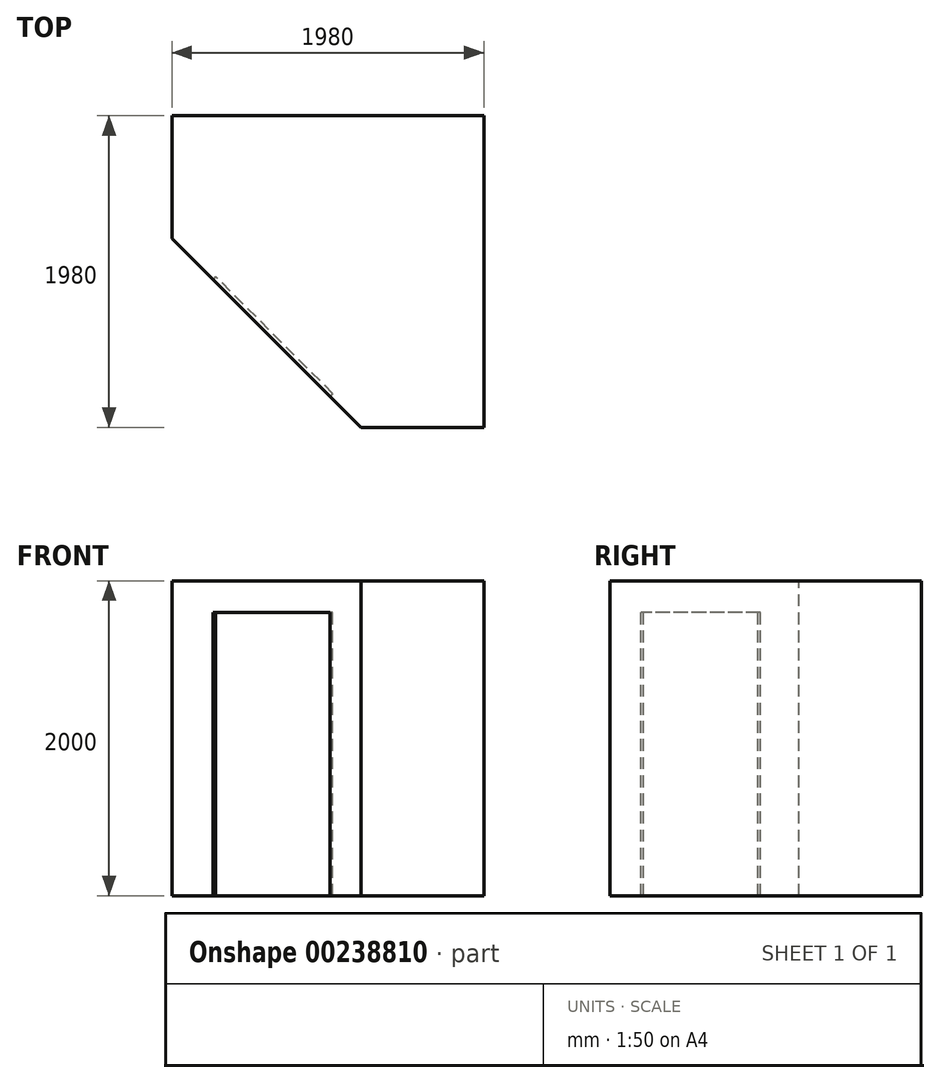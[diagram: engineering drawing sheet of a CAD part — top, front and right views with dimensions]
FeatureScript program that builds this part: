
annotation { "Feature Type Name" : "Feature", "Feature Type Description" : "" }
export const myFeature = defineFeature(function(context is Context, id is Id, definition is map)
    precondition{}
    {
        {
            var Q0;
            Q0=qCreatedBy(makeId("Top.planeOp"),FACE);
            var sketch = newSketch(context, id + "F0", { "sketchPlane" : qUnion([Q0])});
            skLineSegment(sketch, "E0.bottom", {"start": v(0, 0) * mm, "end": v(1980, 0) * mm});
            skLineSegment(sketch, "E0.top", {"start": v(0, 1980) * mm, "end": v(1980, 1980) * mm});
            skLineSegment(sketch, "E0.left", {"start": v(0, 0) * mm, "end": v(0, 1980) * mm});
            skLineSegment(sketch, "E0.right", {"start": v(1980, 0) * mm, "end": v(1980, 1980) * mm});
            skSolve(sketch);
        }
        {
            var Q0;
            Q0 = qSketchRegion(id + "F0", true);
            extrude(context, id + "F1", {"entities" : qUnion([Q0]), "depth" : 2000 * mm});
        }
        {
            var Q0;
            Q0=makeQuery(id+"F1.opExtrude","SWEPT_EDGE",EDGE,{"disambiguationData":[OSD([sQuery(id+"F0.wireOp",EDGE,"E0.bottom"),sQuery(id+"F0.wireOp",EDGE,"E0.left")])]});
            chamfer(context, id + "F2", {"entities" : qUnion([Q0]), "width" : 1200 * mm, "tangentPropagation" : true});
        }
        {
            var Q0;
            Q0=makeQuery(id+"F2.opChamfer","BLEND_FACE",FACE,{"disambiguationData":[OSD([sQuery(id+"F0.wireOp",EDGE,"E0.bottom"),sQuery(id+"F0.wireOp",EDGE,"E0.left")])]});
            var sketch = newSketch(context, id + "F3", { "sketchPlane" : qUnion([Q0])});
            skLineSegment(sketch, "E1.bottom", {"start": v(-480.82, 0) * mm, "end": v(569.18, 0) * mm});
            skLineSegment(sketch, "E1.top", {"start": v(-480.82, 1800) * mm, "end": v(569.18, 1800) * mm});
            skLineSegment(sketch, "E1.left", {"start": v(-480.82, 0) * mm, "end": v(-480.82, 1800) * mm});
            skLineSegment(sketch, "E1.right", {"start": v(569.18, 0) * mm, "end": v(569.18, 1800) * mm});
            skSolve(sketch);
        }
        {
            var Q0;
            Q0 = qSketchRegion(id + "F3", true);
            extrude(context, id + "F4", {"entities" : qUnion([Q0]), "operationType" : NewBodyOperationType.REMOVE, "oppositeDirection" : true, "depth" : 25 * mm});
        }
    });
